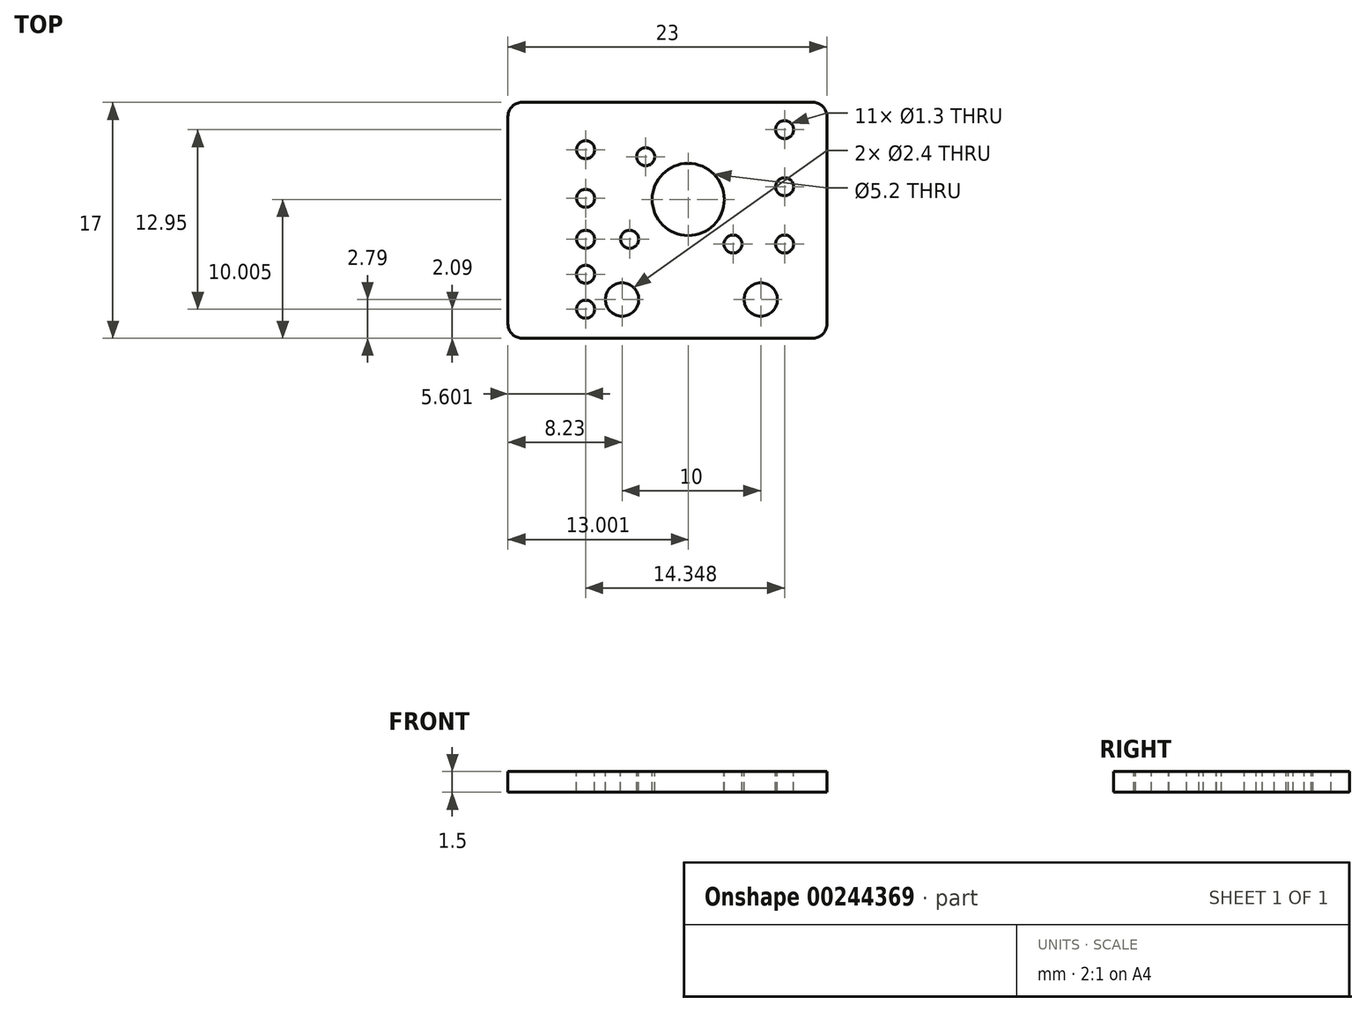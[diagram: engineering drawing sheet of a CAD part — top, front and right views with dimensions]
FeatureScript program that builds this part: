
annotation { "Feature Type Name" : "Feature", "Feature Type Description" : "" }
export const myFeature = defineFeature(function(context is Context, id is Id, definition is map)
    precondition{}
    {
        {
            var Q0;
            Q0=qCreatedBy(makeId("Top.planeOp"),FACE);
            var sketch = newSketch(context, id + "F0", { "sketchPlane" : qUnion([Q0])});
            skLineSegment(sketch, "E0", {"start": v(-12.23, 7.21) * mm, "end": v(8.77, 7.21) * mm});
            skLineSegment(sketch, "E1", {"start": v(9.77, 6.21) * mm, "end": v(9.77, -8.79) * mm});
            skLineSegment(sketch, "E2", {"start": v(8.77, -9.79) * mm, "end": v(-12.23, -9.79) * mm});
            skLineSegment(sketch, "E3", {"start": v(-13.23, -8.79) * mm, "end": v(-13.23, 6.21) * mm});
            skPoint(sketch, "E4.newPointA", {"position": v(-13.23, 7.73) * mm});
            skArc(sketch, "E4.filletArc", {"start": v(-12.23, 7.21) * mm, "mid": v(-12.94, 6.92) * mm, "end": v(-13.23, 6.21) * mm});
            skArc(sketch, "E5.filletArc", {"start": v(9.77, 6.21) * mm, "mid": v(9.48, 6.92) * mm, "end": v(8.77, 7.21) * mm});
            skArc(sketch, "E6.filletArc", {"start": v(8.77, -9.79) * mm, "mid": v(9.48, -9.5) * mm, "end": v(9.77, -8.79) * mm});
            skPoint(sketch, "E7.visualSharp", {"position": v(-13.23, -9.79) * mm});
            skArc(sketch, "E7.filletArc", {"start": v(-13.23, -8.79) * mm, "mid": v(-12.94, -9.5) * mm, "end": v(-12.23, -9.79) * mm});
            skSolve(sketch);
        }
        {
            var Q0;
            Q0=qSketchRegion(id+"F0",true);
            extrude(context, id + "F1", {"entities" : qUnion([Q0]), "depth" : 1.5 * mm});
        }
        {
            var Q0;
            Q0=makeQuery(id+"F1.opExtrude","CAP_FACE",FACE,{"disambiguationData":[OSD([sQuery(id+"F0.wireOp",EDGE,"E0"),sQuery(id+"F0.wireOp",EDGE,"E1"),sQuery(id+"F0.wireOp",EDGE,"BHbmHS0J-i3Xx-4d6p-fsTU-bkkSeQT16j2F"),sQuery(id+"F0.wireOp",EDGE,"Pxyrazc0-ufuX-MaGq-Lisa-V6kmK2EmZJ5E")])],"isStart":false});
            var sketch = newSketch(context, id + "F2", { "sketchPlane" : qUnion([Q0])});
            skCircle(sketch, "E8", {"center": v(-0.23, 0.21) * mm, "radius": 2.6 * mm});
            skSolve(sketch);
        }
        {
            var Q0;
            Q0=makeQuery(id+"F1.opExtrude","CAP_FACE",FACE,{"disambiguationData":[OSD([sQuery(id+"F0.wireOp",EDGE,"0JzyJq7d-DXwQ-p0i9-ll30-icSSdf44xIEe"),sQuery(id+"F0.wireOp",EDGE,"E0"),sQuery(id+"F0.wireOp",EDGE,"E1")])],"isStart":false});
            var sketch = newSketch(context, id + "F3", { "sketchPlane" : qUnion([Q0])});
            skCircle(sketch, "E9", {"center": v(-5, -7) * mm, "radius": 1.2 * mm});
            skCircle(sketch, "E10.MirrorC", {"center": v(5, -7) * mm, "radius": 1.2 * mm});
            skSolve(sketch);
        }
        {
            var Q0;
            Q0=qSketchRegion(id+"F3",true);
            extrude(context, id + "F4", {"entities" : qUnion([Q0]), "operationType" : NewBodyOperationType.REMOVE, "oppositeDirection" : true, "depth" : 4 * mm});
        }
        {
            var Q0;
            Q0=makeQuery(id+"F1.opExtrude","CAP_FACE",FACE,{"disambiguationData":[OSD([sQuery(id+"F0.wireOp",EDGE,"0JzyJq7d-DXwQ-p0i9-ll30-icSSdf44xIEe"),sQuery(id+"F0.wireOp",EDGE,"E0"),sQuery(id+"F0.wireOp",EDGE,"E1")])],"isStart":false});
            var sketch = newSketch(context, id + "F5", { "sketchPlane" : qUnion([Q0])});
            skCircle(sketch, "E11", {"center": v(-7.63, -7.7) * mm, "radius": 0.65 * mm});
            skCircle(sketch, "E12.1.0.0", {"center": v(-7.63, -5.18) * mm, "radius": 0.65 * mm});
            skCircle(sketch, "E12.2.0.0", {"center": v(-7.63, -2.65) * mm, "radius": 0.65 * mm});
            skLineSegment(sketch, "E12.direction1", {"start": v(-7.63, -7.7) * mm, "end": v(-7.63, -5.18) * mm, "construction": true});
            skCircle(sketch, "E13", {"center": v(-4.46, -2.65) * mm, "radius": 0.65 * mm});
            skSolve(sketch);
        }
        {
            var Q0;
            Q0=qSketchRegion(id+"F5",true);
            extrude(context, id + "F6", {"entities" : qUnion([Q0]), "operationType" : NewBodyOperationType.REMOVE, "oppositeDirection" : true, "depth" : 25 * mm});
        }
        {
            var Q0;
            Q0=makeQuery(id+"F1.opExtrude","CAP_FACE",FACE,{"disambiguationData":[OSD([sQuery(id+"F0.wireOp",EDGE,"0JzyJq7d-DXwQ-p0i9-ll30-icSSdf44xIEe"),sQuery(id+"F0.wireOp",EDGE,"E0"),sQuery(id+"F0.wireOp",EDGE,"E1")])],"isStart":false});
            var sketch = newSketch(context, id + "F7", { "sketchPlane" : qUnion([Q0])});
            skCircle(sketch, "E14", {"center": v(-2.5, -4) * mm, "radius": 0.65 * mm, "construction": true});
            skCircle(sketch, "E15.1.0.0", {"center": v(-2.5, -10.5) * mm, "radius": 0.65 * mm, "construction": true});
            skCircle(sketch, "E16.MirrorC", {"center": v(6.72, 5.25) * mm, "radius": 0.65 * mm});
            skCircle(sketch, "E17.MirrorC", {"center": v(6.72, 1.13) * mm, "radius": 0.65 * mm});
            skCircle(sketch, "E18", {"center": v(6.72, -3) * mm, "radius": 0.65 * mm});
            skSolve(sketch);
        }
        {
            var Q0;
            Q0=qSketchRegion(id+"F7",true);
            extrude(context, id + "F8", {"entities" : qUnion([Q0]), "operationType" : NewBodyOperationType.REMOVE, "oppositeDirection" : true, "depth" : 25 * mm});
        }
        {
            var Q0;
            Q0=makeQuery(id+"F1.opExtrude","CAP_FACE",FACE,{"disambiguationData":[OSD([sQuery(id+"F0.wireOp",EDGE,"0JzyJq7d-DXwQ-p0i9-ll30-icSSdf44xIEe"),sQuery(id+"F0.wireOp",EDGE,"E0"),sQuery(id+"F0.wireOp",EDGE,"E1")])],"isStart":false});
            var sketch = newSketch(context, id + "F9", { "sketchPlane" : qUnion([Q0])});
            skCircle(sketch, "E19.0", {"center": v(-7.63, -2.65) * mm, "radius": 0.65 * mm, "construction": true});
            skCircle(sketch, "E20.0", {"center": v(-7.63, -7.7) * mm, "radius": 0.65 * mm, "construction": true});
            skCircle(sketch, "E21.MirrorC", {"center": v(-7.63, 3.8) * mm, "radius": 0.65 * mm});
            skCircle(sketch, "E22.MirrorC", {"center": v(-7.63, 0.3) * mm, "radius": 0.65 * mm});
            skSolve(sketch);
        }
        {
            var Q0;
            Q0=qSketchRegion(id+"F9",true);
            var Q1;
            Q1=sQuery(id+"F9.wireOp",EDGE,"E19.0");
            var Q2;
            Q2=sQuery(id+"F9.wireOp",EDGE,"E20.0");
            extrude(context, id + "F10", {"entities" : qUnion([Q0]), "operationType" : NewBodyOperationType.REMOVE, "surfaceEntities" : qUnion([Q1, Q2]), "oppositeDirection" : true, "depth" : 25 * mm});
        }
        {
            var Q0;
            Q0=makeQuery(id+"F1.opExtrude","CAP_FACE",FACE,{"disambiguationData":[OSD([sQuery(id+"F0.wireOp",EDGE,"0JzyJq7d-DXwQ-p0i9-ll30-icSSdf44xIEe"),sQuery(id+"F0.wireOp",EDGE,"E0"),sQuery(id+"F0.wireOp",EDGE,"E1")])],"isStart":false});
            var sketch = newSketch(context, id + "F11", { "sketchPlane" : qUnion([Q0])});
            skCircle(sketch, "E23", {"center": v(3, -3) * mm, "radius": 0.65 * mm});
            skCircle(sketch, "E24.MirrorC", {"center": v(-3.3, 3.3) * mm, "radius": 0.65 * mm});
            skSolve(sketch);
        }
        {
            var Q0;
            Q0=qSketchRegion(id+"F3",true);
            extrude(context, id + "F12", {"entities" : qUnion([Q0]), "operationType" : NewBodyOperationType.REMOVE, "oppositeDirection" : true, "depth" : 25 * mm});
        }
        {
            var Q0;
            Q0=qSketchRegion(id+"F2",true);
            extrude(context, id + "F13", {"entities" : qUnion([Q0]), "operationType" : NewBodyOperationType.REMOVE, "oppositeDirection" : true, "depth" : 25 * mm});
        }
        {
            var Q0;
            Q0=qSketchRegion(id+"F11",true);
            extrude(context, id + "F14", {"entities" : qUnion([Q0]), "operationType" : NewBodyOperationType.REMOVE, "oppositeDirection" : true, "depth" : 25 * mm});
        }
    });
